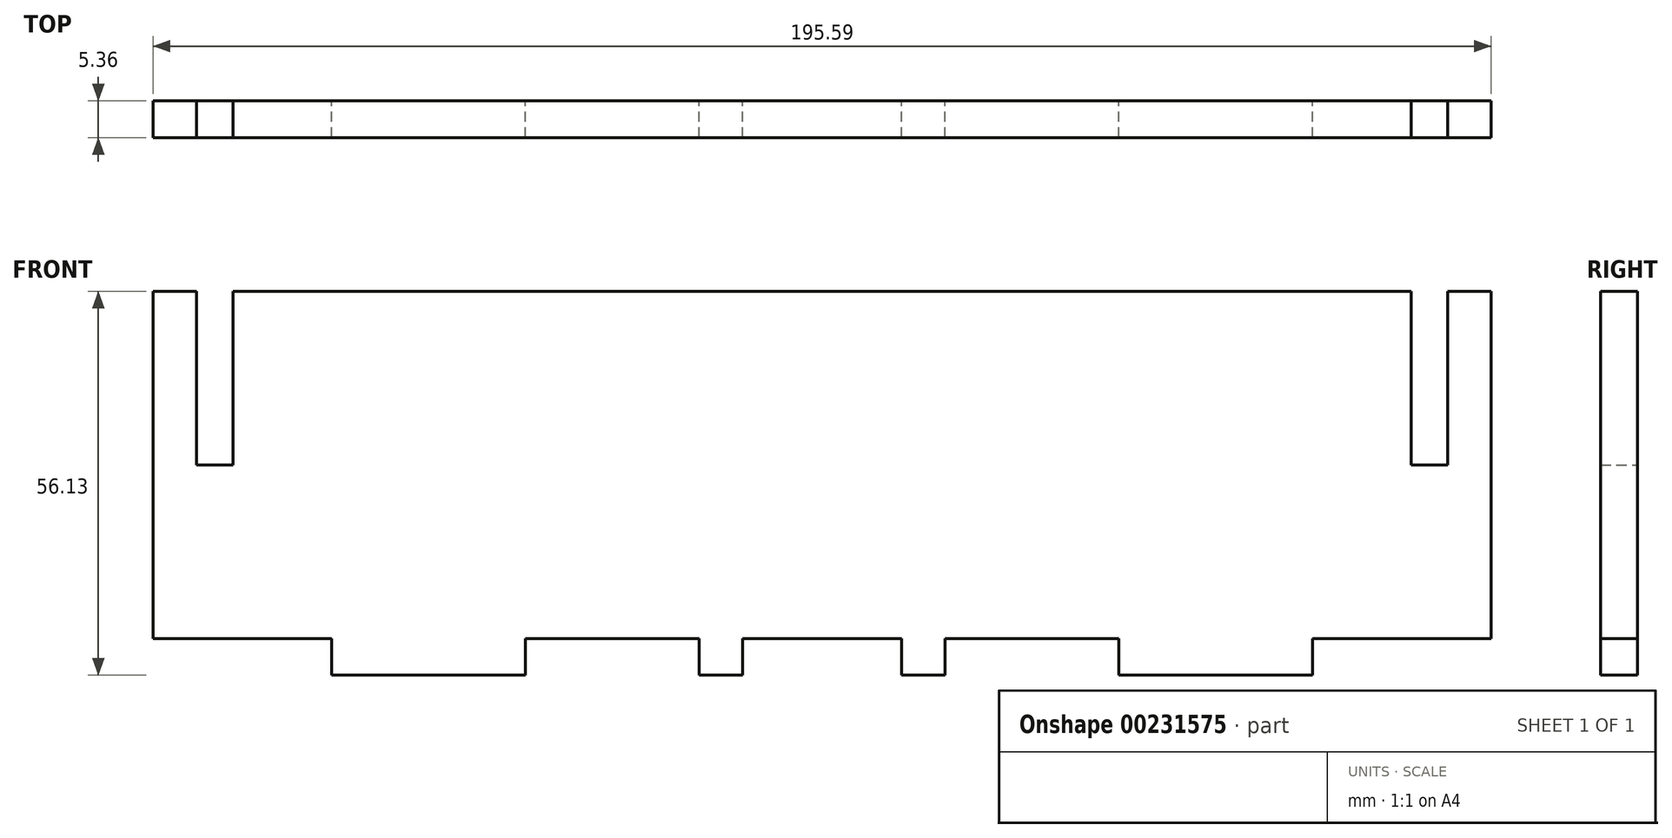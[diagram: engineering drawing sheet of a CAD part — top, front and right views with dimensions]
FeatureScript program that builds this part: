
annotation { "Feature Type Name" : "Feature", "Feature Type Description" : "" }
export const myFeature = defineFeature(function(context is Context, id is Id, definition is map)
    precondition{}
    {
        {
            var Q0;
            Q0=qCreatedBy(makeId("Front.planeOp"),FACE);
            var sketch = newSketch(context, id + "F0", { "sketchPlane" : qUnion([Q0])});
            skLineSegment(sketch, "E0.bottom", {"start": v(0, 0) * mm, "end": v(195.59, 0) * mm});
            skLineSegment(sketch, "E0.top", {"start": v(0, 50.8) * mm, "end": v(195.59, 50.8) * mm});
            skLineSegment(sketch, "E0.left", {"start": v(0, 0) * mm, "end": v(0, 50.8) * mm});
            skLineSegment(sketch, "E0.right", {"start": v(195.59, 0) * mm, "end": v(195.59, 50.8) * mm});
            skPoint(sketch, "E1", {"position": v(97.8, 50.8) * mm});
            skLineSegment(sketch, "E2", {"start": v(86.16, 50.8) * mm, "end": v(86.16, 0) * mm, "construction": true});
            skLineSegment(sketch, "E3", {"start": v(109.43, 50.8) * mm, "end": v(109.43, 0) * mm, "construction": true});
            skLineSegment(sketch, "E4.bottom", {"start": v(86.16, 50.8) * mm, "end": v(26.09, 50.8) * mm});
            skLineSegment(sketch, "E4.top", {"start": v(86.16, 56.13) * mm, "end": v(26.09, 56.13) * mm});
            skLineSegment(sketch, "E4.left", {"start": v(86.16, 50.8) * mm, "end": v(86.16, 56.13) * mm});
            skLineSegment(sketch, "E4.right", {"start": v(26.09, 50.8) * mm, "end": v(26.09, 56.13) * mm});
            skPoint(sketch, "E5.oppositeSnap0", {"position": v(56.12, 56.13) * mm});
            skLineSegment(sketch, "E5.bottom", {"start": v(109.43, 50.8) * mm, "end": v(169.5, 50.8) * mm});
            skLineSegment(sketch, "E5.top", {"start": v(109.43, 56.13) * mm, "end": v(169.5, 56.13) * mm});
            skLineSegment(sketch, "E5.left", {"start": v(109.43, 50.8) * mm, "end": v(109.43, 56.13) * mm});
            skLineSegment(sketch, "E5.right", {"start": v(169.5, 50.8) * mm, "end": v(169.5, 56.13) * mm});
            skLineSegment(sketch, "E6.bottom", {"start": v(86.16, 0) * mm, "end": v(26.09, 0) * mm});
            skLineSegment(sketch, "E6.top", {"start": v(86.16, -5.33) * mm, "end": v(26.09, -5.33) * mm});
            skLineSegment(sketch, "E6.left", {"start": v(86.16, 0) * mm, "end": v(86.16, -5.33) * mm});
            skLineSegment(sketch, "E6.right", {"start": v(26.09, 0) * mm, "end": v(26.09, -5.33) * mm});
            skLineSegment(sketch, "E7.bottom", {"start": v(109.43, 0) * mm, "end": v(169.5, 0) * mm});
            skLineSegment(sketch, "E7.top", {"start": v(109.43, -5.33) * mm, "end": v(169.5, -5.33) * mm});
            skLineSegment(sketch, "E7.left", {"start": v(109.43, 0) * mm, "end": v(109.43, -5.33) * mm});
            skLineSegment(sketch, "E7.right", {"start": v(169.5, 0) * mm, "end": v(169.5, -5.33) * mm});
            skLineSegment(sketch, "E8.bottom", {"start": v(6.35, 50.8) * mm, "end": v(11.68, 50.8) * mm});
            skLineSegment(sketch, "E8.top", {"start": v(6.35, 25.4) * mm, "end": v(11.68, 25.4) * mm});
            skLineSegment(sketch, "E8.left", {"start": v(6.35, 50.8) * mm, "end": v(6.35, 25.4) * mm});
            skLineSegment(sketch, "E8.right", {"start": v(11.68, 50.8) * mm, "end": v(11.68, 25.4) * mm});
            skLineSegment(sketch, "E9.bottom", {"start": v(183.9, 50.8) * mm, "end": v(189.24, 50.8) * mm});
            skLineSegment(sketch, "E9.top", {"start": v(183.9, 25.4) * mm, "end": v(189.24, 25.4) * mm});
            skLineSegment(sketch, "E9.left", {"start": v(183.9, 50.8) * mm, "end": v(183.9, 25.4) * mm});
            skLineSegment(sketch, "E9.right", {"start": v(189.24, 50.8) * mm, "end": v(189.24, 25.4) * mm});
            skLineSegment(sketch, "E10.bottom", {"start": v(79.8, -5.33) * mm, "end": v(54.4, -5.33) * mm});
            skLineSegment(sketch, "E10.top", {"start": v(79.8, 0) * mm, "end": v(54.4, 0) * mm});
            skLineSegment(sketch, "E10.left", {"start": v(79.8, -5.33) * mm, "end": v(79.8, 0) * mm});
            skLineSegment(sketch, "E10.right", {"start": v(54.4, -5.33) * mm, "end": v(54.4, 0) * mm});
            skLineSegment(sketch, "E11.bottom", {"start": v(115.78, -5.33) * mm, "end": v(141.18, -5.33) * mm});
            skLineSegment(sketch, "E11.top", {"start": v(115.78, 0) * mm, "end": v(141.18, 0) * mm});
            skLineSegment(sketch, "E11.left", {"start": v(115.78, -5.33) * mm, "end": v(115.78, 0) * mm});
            skLineSegment(sketch, "E11.right", {"start": v(141.18, -5.33) * mm, "end": v(141.18, 0) * mm});
            skSolve(sketch);
        }
        {
            var Q0;
            Q0=makeQuery(id+"F0.imprint","IMPRINT",FACE,{"disambiguationData":[TD([[makeQuery(id+"F0.imprint","IMPRINT",EDGE,{"derivedFrom":sQuery(id+"F0.wireOp",EDGE,"E4.bottom")}),-1.0]])]});
            var Q1;
            Q1=makeQuery(id+"F0.imprint","IMPRINT",FACE,{"disambiguationData":[TD([[makeQuery(id+"F0.imprint","IMPRINT",EDGE,{"derivedFrom":sQuery(id+"F0.wireOp",EDGE,"E5.bottom")}),1.0]])]});
            var Q2;
            {var subQ15=sQuery(id+"F0.wireOp",EDGE,"E0.left");Q2=makeQuery(id+"F0.imprint","IMPRINT",FACE,{"disambiguationData":[TD([[makeQuery(id+"F0.imprint","IMPRINT",EDGE,{"derivedFrom":subQ15}),-1.0]])]});}
            var Q3;
            {var subQ0=sQuery(id+"F0.wireOp",EDGE,"E6.right");Q3=makeQuery(id+"F0.imprint","IMPRINT",FACE,{"disambiguationData":[TD([[makeQuery(id+"F0.imprint","IMPRINT",EDGE,{"derivedFrom":subQ0}),1.0]])]});}
            var Q4;
            {var subQ0=sQuery(id+"F0.wireOp",EDGE,"E6.left");Q4=makeQuery(id+"F0.imprint","IMPRINT",FACE,{"disambiguationData":[TD([[makeQuery(id+"F0.imprint","IMPRINT",EDGE,{"derivedFrom":subQ0}),-1.0]])]});}
            var Q5;
            {var subQ0=sQuery(id+"F0.wireOp",EDGE,"E7.left");Q5=makeQuery(id+"F0.imprint","IMPRINT",FACE,{"disambiguationData":[TD([[makeQuery(id+"F0.imprint","IMPRINT",EDGE,{"derivedFrom":subQ0}),1.0]])]});}
            var Q6;
            {var subQ0=sQuery(id+"F0.wireOp",EDGE,"E7.right");Q6=makeQuery(id+"F0.imprint","IMPRINT",FACE,{"disambiguationData":[TD([[makeQuery(id+"F0.imprint","IMPRINT",EDGE,{"derivedFrom":subQ0}),-1.0]])]});}
            extrude(context, id + "F1", {"entities" : qUnion([Q0, Q1, Q2, Q3, Q4, Q5, Q6]), "depth" : 5.36 * mm});
        }
    });
